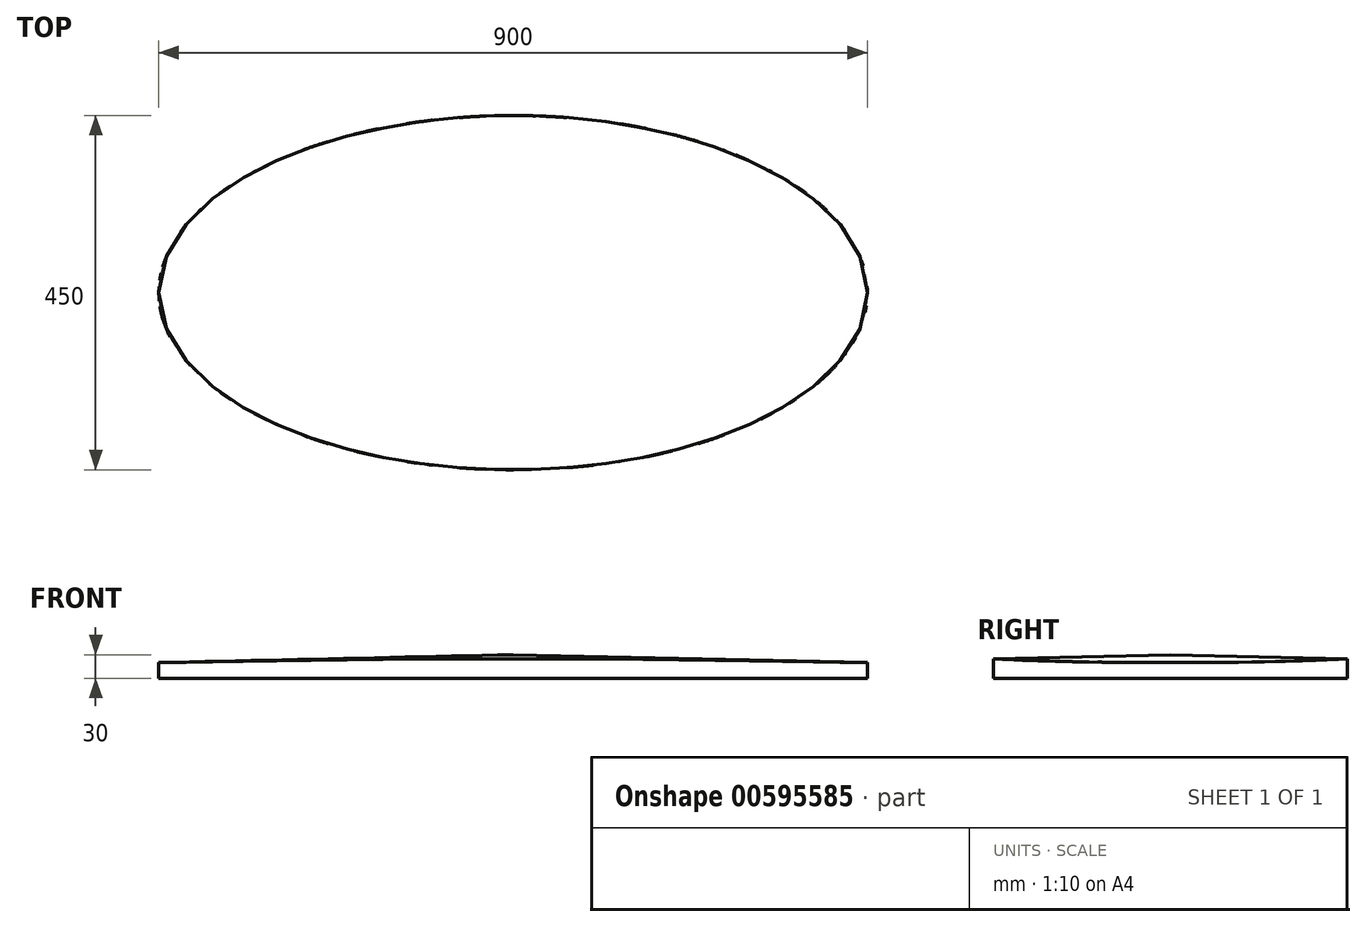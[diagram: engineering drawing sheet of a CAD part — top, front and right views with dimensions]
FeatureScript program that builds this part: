
annotation { "Feature Type Name" : "Feature", "Feature Type Description" : "" }
export const myFeature = defineFeature(function(context is Context, id is Id, definition is map)
    precondition{}
    {
        {
            var Q0;
            Q0=qCreatedBy(makeId("Front.planeOp"),FACE);
            var sketch = newSketch(context, id + "F0", { "sketchPlane" : qUnion([Q0])});
            skLineSegment(sketch, "E0.MirrorCS", {"start": v(0, 0) * mm, "end": v(-450, 0) * mm});
            skLineSegment(sketch, "E1.MirrorCS", {"start": v(-450, 0) * mm, "end": v(-450, 20) * mm});
            skLineSegment(sketch, "E2.MirrorCS", {"start": v(0, 30) * mm, "end": v(-450, 20) * mm});
            skLineSegment(sketch, "E3", {"start": v(0, 30) * mm, "end": v(0, 0) * mm});
            skSolve(sketch);
        }
        {
            var Q0;
            Q0 = qSketchRegion(id + "F0", true);
            var Q1;
            Q1=sQuery(id+"F0.wireOp",EDGE,"E3");
            revolve(context, id + "F1", {"entities" : qUnion([Q0]), "axis" : qUnion([Q1]), "revolveType" : RevolveType.FULL});
        }
        {
            var Q0;
            Q0=qCreatedBy(makeId("Top.planeOp"),FACE);
            cPlane(context, id + "F2", {"entities" : qUnion([Q0]), "cplaneType" : CPlaneType.OFFSET, "offset" : 30 * mm, "width" : 150 * mm, "height" : 150 * mm});
        }
        {
            var Q0;
            Q0=qCreatedBy(id+"F2.planeOp",FACE);
            var sketch = newSketch(context, id + "F3", { "sketchPlane" : qUnion([Q0])});
            skEllipse(sketch, "E4", {"center": v(0, 0) * mm, "majorRadius": 450 * mm, "minorRadius": 225 * mm, "majorAxis": v(-1, 0)});
            skFitSpline(sketch, "E5.0", {"points": [v(-349.99, 0.63) * mm, v(-350, 0) * mm, v(-349.99, -0.63) * mm, v(-349.93, -1.5) * mm, v(-349.75, -2.7) * mm, v(-349.3, -4.53) * mm, v(-348.5, -6.88) * mm, v(-347.2, -9.82) * mm, v(-345.23, -13.39) * mm, v(-342.5, -17.54) * mm, v(-338.9, -22.23) * mm, v(-334.34, -27.39) * mm, v(-328.8, -32.92) * mm, v(-322.2, -38.75) * mm, v(-314.58, -44.8) * mm, v(-305.9, -50.99) * mm, v(-297.8, -56.2) * mm, v(-290.8, -60.36) * mm, v(-285.29, -63.48) * mm, v(-279.53, -66.58) * mm, v(-273.52, -69.66) * mm, v(-267.27, -72.7) * mm, v(-260.82, -75.7) * mm, v(-254.17, -78.64) * mm, v(-245.03, -82.48) * mm, v(-233.13, -87.11) * mm, v(-218.14, -92.38) * mm, v(-202.49, -97.33) * mm, v(-180.79, -103.47) * mm, v(-152.24, -110.22) * mm, v(-122.12, -115.62) * mm, v(-97.27, -119.07) * mm, v(-78.3, -121.2) * mm, v(-59.05, -122.89) * mm, v(-42.8, -123.9) * mm, v(-29.7, -124.47) * mm, v(-19.84, -124.77) * mm, v(-11.59, -124.93) * mm, v(-4.97, -124.99) * mm, v(0, -125) * mm, v(4.97, -124.99) * mm, v(11.59, -124.93) * mm, v(19.84, -124.77) * mm, v(29.7, -124.47) * mm, v(42.8, -123.9) * mm, v(59.05, -122.89) * mm, v(78.3, -121.2) * mm, v(97.27, -119.07) * mm, v(122.12, -115.62) * mm, v(152.24, -110.22) * mm, v(180.79, -103.47) * mm, v(202.49, -97.33) * mm, v(218.14, -92.38) * mm, v(233.13, -87.11) * mm, v(245.03, -82.48) * mm, v(254.17, -78.64) * mm, v(260.82, -75.7) * mm, v(267.27, -72.7) * mm, v(273.52, -69.66) * mm, v(279.53, -66.58) * mm, v(285.29, -63.48) * mm, v(290.8, -60.36) * mm, v(297.8, -56.2) * mm, v(305.9, -50.99) * mm, v(314.58, -44.8) * mm, v(322.2, -38.75) * mm, v(328.8, -32.92) * mm, v(334.34, -27.39) * mm, v(338.9, -22.23) * mm, v(342.5, -17.54) * mm, v(345.23, -13.39) * mm, v(347.2, -9.82) * mm, v(348.5, -6.88) * mm, v(349.3, -4.53) * mm, v(349.75, -2.7) * mm, v(349.93, -1.5) * mm, v(349.99, -0.63) * mm, v(350, 0) * mm, v(349.99, 0.63) * mm, v(349.93, 1.5) * mm, v(349.75, 2.7) * mm, v(349.3, 4.53) * mm, v(348.5, 6.88) * mm, v(347.2, 9.82) * mm, v(345.23, 13.39) * mm, v(342.5, 17.54) * mm, v(338.9, 22.23) * mm, v(334.34, 27.39) * mm, v(328.8, 32.92) * mm, v(322.2, 38.75) * mm, v(314.58, 44.8) * mm, v(305.9, 50.99) * mm, v(297.8, 56.2) * mm, v(290.8, 60.36) * mm, v(285.29, 63.48) * mm, v(279.53, 66.58) * mm, v(273.52, 69.66) * mm, v(267.27, 72.7) * mm, v(260.82, 75.7) * mm, v(254.17, 78.64) * mm, v(245.03, 82.48) * mm, v(233.13, 87.11) * mm, v(218.14, 92.38) * mm, v(202.49, 97.33) * mm, v(180.79, 103.47) * mm, v(152.24, 110.22) * mm, v(122.12, 115.62) * mm, v(97.27, 119.07) * mm, v(78.3, 121.2) * mm, v(59.05, 122.89) * mm, v(42.8, 123.9) * mm, v(29.7, 124.47) * mm, v(19.84, 124.77) * mm, v(11.59, 124.93) * mm, v(4.97, 124.99) * mm, v(0, 125) * mm, v(-4.97, 124.99) * mm, v(-11.59, 124.93) * mm, v(-19.84, 124.77) * mm, v(-29.7, 124.47) * mm, v(-42.8, 123.9) * mm, v(-59.05, 122.89) * mm, v(-78.3, 121.2) * mm, v(-97.27, 119.07) * mm, v(-122.12, 115.62) * mm, v(-152.24, 110.22) * mm, v(-180.79, 103.47) * mm, v(-202.49, 97.33) * mm, v(-218.14, 92.38) * mm, v(-233.13, 87.11) * mm, v(-245.03, 82.48) * mm, v(-254.17, 78.64) * mm, v(-260.82, 75.7) * mm, v(-267.27, 72.7) * mm, v(-273.52, 69.66) * mm, v(-279.53, 66.58) * mm, v(-285.29, 63.48) * mm, v(-290.8, 60.36) * mm, v(-297.8, 56.2) * mm, v(-305.9, 50.99) * mm, v(-314.58, 44.8) * mm, v(-322.2, 38.75) * mm, v(-328.8, 32.92) * mm, v(-334.34, 27.39) * mm, v(-338.9, 22.23) * mm, v(-342.5, 17.54) * mm, v(-345.23, 13.39) * mm, v(-347.2, 9.82) * mm, v(-348.5, 6.88) * mm, v(-349.3, 4.53) * mm, v(-349.75, 2.7) * mm, v(-349.93, 1.5) * mm, v(-349.99, 0.63) * mm, v(-350, 0) * mm, v(-349.99, -0.63) * mm, v(-349.99, 0.63) * mm]});
            skSolve(sketch);
        }
        {
            var Q0;
            Q0 = qSketchRegion(id + "F3", true);
            extrude(context, id + "F4", {"entities" : qUnion([Q0]), "operationType" : NewBodyOperationType.INTERSECT, "oppositeDirection" : true, "depth" : 40 * mm, "offsetDistance" : 25 * mm});
        }
    });
